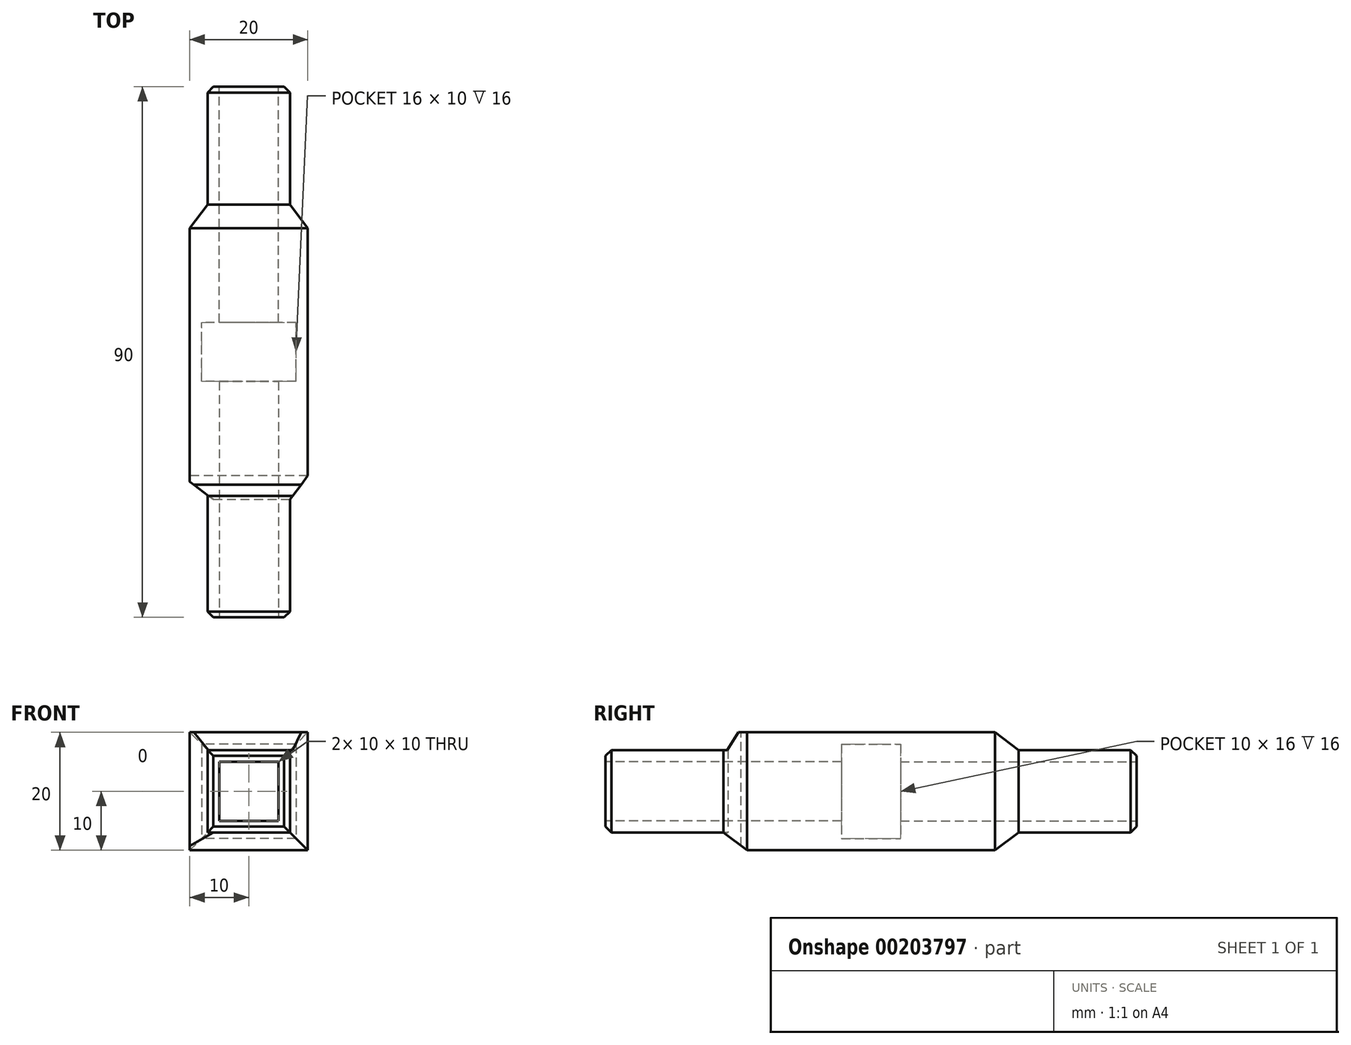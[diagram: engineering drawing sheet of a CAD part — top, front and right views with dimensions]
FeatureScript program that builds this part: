
annotation { "Feature Type Name" : "Feature", "Feature Type Description" : "" }
export const myFeature = defineFeature(function(context is Context, id is Id, definition is map)
    precondition{}
    {
        {
            var Q0;
            Q0=qCreatedBy(makeId("Front.planeOp"),FACE);
            var sketch = newSketch(context, id + "F0", { "sketchPlane" : qUnion([Q0])});
            skLineSegment(sketch, "E0.bottom", {"start": v(10, 10) * mm, "end": v(-10, 10) * mm});
            skLineSegment(sketch, "E0.top", {"start": v(10, -10) * mm, "end": v(-10, -10) * mm});
            skLineSegment(sketch, "E0.left", {"start": v(10, 10) * mm, "end": v(10, -10) * mm});
            skLineSegment(sketch, "E0.right", {"start": v(-10, 10) * mm, "end": v(-10, -10) * mm});
            skPoint(sketch, "E0.middle", {"position": v(0, 0) * mm});
            skLineSegment(sketch, "E1.0", {"start": v(-8, 8) * mm, "end": v(-8, -8) * mm});
            skLineSegment(sketch, "E1.1", {"start": v(8, 8) * mm, "end": v(-8, 8) * mm});
            skLineSegment(sketch, "E1.2", {"start": v(8, 8) * mm, "end": v(8, -8) * mm});
            skLineSegment(sketch, "E1.3", {"start": v(8, -8) * mm, "end": v(-8, -8) * mm});
            skSolve(sketch);
        }
        {
            var Q0;
            Q0=makeQuery(id+"F0.imprint","IMPRINT",FACE,{"disambiguationData":[TD([[makeQuery(id+"F0.imprint","IMPRINT",EDGE,{"derivedFrom":sQuery(id+"F0.wireOp",EDGE,"E0.bottom")}),1.0]])]});
            extrude(context, id + "F1", {"entities" : qUnion([Q0]), "depth" : 50 * mm, "symmetric" : true});
        }
        {
            var Q0;
            Q0=makeQuery(id+"F1.opExtrude","CAP_FACE",FACE,{"disambiguationData":[OSD([sQuery(id+"F0.wireOp",EDGE,"E0.bottom"),sQuery(id+"F0.wireOp",EDGE,"E0.top"),sQuery(id+"F0.wireOp",EDGE,"E0.left"),sQuery(id+"F0.wireOp",EDGE,"E0.right"),sQuery(id+"F0.wireOp",EDGE,"E1.0"),sQuery(id+"F0.wireOp",EDGE,"E1.1"),sQuery(id+"F0.wireOp",EDGE,"E1.2"),sQuery(id+"F0.wireOp",EDGE,"E1.3")])],"isStart":false});
            var sketch = newSketch(context, id + "F2", { "sketchPlane" : qUnion([Q0])});
            skLineSegment(sketch, "E2.bottom", {"start": v(-8, 8) * mm, "end": v(8, 8) * mm});
            skLineSegment(sketch, "E2.top", {"start": v(-8, -8) * mm, "end": v(8, -8) * mm});
            skLineSegment(sketch, "E2.left", {"start": v(-8, 8) * mm, "end": v(-8, -8) * mm});
            skLineSegment(sketch, "E2.right", {"start": v(8, 8) * mm, "end": v(8, -8) * mm});
            skPoint(sketch, "E2.middle", {"position": v(0, 0) * mm});
            skLineSegment(sketch, "E3.0", {"start": v(-5, 5) * mm, "end": v(5, 5) * mm});
            skLineSegment(sketch, "E3.1", {"start": v(-5, 5) * mm, "end": v(-5, -5) * mm});
            skLineSegment(sketch, "E3.2", {"start": v(-5, -5) * mm, "end": v(5, -5) * mm});
            skLineSegment(sketch, "E3.3", {"start": v(5, 5) * mm, "end": v(5, -5) * mm});
            skSolve(sketch);
        }
        {
            var Q0;
            Q0=makeQuery(id+"F2.imprint","IMPRINT",FACE,{"disambiguationData":[TD([[makeQuery(id+"F2.imprint","IMPRINT",EDGE,{"derivedFrom":sQuery(id+"F2.wireOp",EDGE,"E2.bottom")}),1.0]])]});
            extrude(context, id + "F3", {"entities" : qUnion([Q0]), "operationType" : NewBodyOperationType.ADD, "oppositeDirection" : true, "depth" : 20 * mm});
        }
        {
            var Q0;
            Q0=makeQuery(id+"F3.boolean.opBoolean","MERGE",FACE,{"derivedFrom":[makeQuery(id+"F1.opExtrude","CAP_FACE",FACE,{"disambiguationData":[OSD([sQuery(id+"F0.wireOp",EDGE,"E0.bottom"),sQuery(id+"F0.wireOp",EDGE,"E0.top"),sQuery(id+"F0.wireOp",EDGE,"E0.left"),sQuery(id+"F0.wireOp",EDGE,"E0.right"),sQuery(id+"F0.wireOp",EDGE,"E1.0"),sQuery(id+"F0.wireOp",EDGE,"E1.1"),sQuery(id+"F0.wireOp",EDGE,"E1.2"),sQuery(id+"F0.wireOp",EDGE,"E1.3")])],"isStart":false}),makeQuery(id+"F3.opExtrude","CAP_FACE",FACE,{"disambiguationData":[OSD([sQuery(id+"F2.wireOp",EDGE,"E2.bottom"),sQuery(id+"F2.wireOp",EDGE,"E2.top"),sQuery(id+"F2.wireOp",EDGE,"E2.left"),sQuery(id+"F2.wireOp",EDGE,"E2.right"),sQuery(id+"F2.wireOp",EDGE,"E3.0"),sQuery(id+"F2.wireOp",EDGE,"E3.1"),sQuery(id+"F2.wireOp",EDGE,"E3.2"),sQuery(id+"F2.wireOp",EDGE,"E3.3")])],"isStart":true})]});
            var sketch = newSketch(context, id + "F4", { "sketchPlane" : qUnion([Q0])});
            skLineSegment(sketch, "E4.bottom", {"start": v(-5, 5) * mm, "end": v(5, 5) * mm});
            skLineSegment(sketch, "E4.top", {"start": v(-5, -5) * mm, "end": v(5, -5) * mm});
            skLineSegment(sketch, "E4.left", {"start": v(-5, 5) * mm, "end": v(-5, -5) * mm});
            skLineSegment(sketch, "E4.right", {"start": v(5, 5) * mm, "end": v(5, -5) * mm});
            skPoint(sketch, "E4.middle", {"position": v(0, 0) * mm});
            skLineSegment(sketch, "E5.0", {"start": v(-7, 7) * mm, "end": v(7, 7) * mm});
            skLineSegment(sketch, "E5.1", {"start": v(-7, 7) * mm, "end": v(-7, -7) * mm});
            skLineSegment(sketch, "E5.2", {"start": v(-7, -7) * mm, "end": v(7, -7) * mm});
            skLineSegment(sketch, "E5.3", {"start": v(7, 7) * mm, "end": v(7, -7) * mm});
            skSolve(sketch);
        }
        {
            var Q0;
            Q0=makeQuery(id+"F4.imprint","IMPRINT",FACE,{"disambiguationData":[TD([[makeQuery(id+"F4.imprint","IMPRINT",EDGE,{"derivedFrom":sQuery(id+"F4.wireOp",EDGE,"E4.bottom")}),1.0]])]});
            extrude(context, id + "F5", {"entities" : qUnion([Q0]), "operationType" : NewBodyOperationType.ADD, "depth" : 20 * mm});
        }
        {
            var Q0;
            Q0=makeQuery(id+"F1.opExtrude","CAP_FACE",FACE,{"disambiguationData":[OSD([sQuery(id+"F0.wireOp",EDGE,"E0.bottom"),sQuery(id+"F0.wireOp",EDGE,"E0.top"),sQuery(id+"F0.wireOp",EDGE,"E0.left"),sQuery(id+"F0.wireOp",EDGE,"E0.right"),sQuery(id+"F0.wireOp",EDGE,"E1.0"),sQuery(id+"F0.wireOp",EDGE,"E1.1"),sQuery(id+"F0.wireOp",EDGE,"E1.2"),sQuery(id+"F0.wireOp",EDGE,"E1.3")])],"isStart":true});
            var sketch = newSketch(context, id + "F6", { "sketchPlane" : qUnion([Q0])});
            skLineSegment(sketch, "E6.bottom", {"start": v(-8, 8) * mm, "end": v(8, 8) * mm});
            skLineSegment(sketch, "E6.top", {"start": v(-8, -8) * mm, "end": v(8, -8) * mm});
            skLineSegment(sketch, "E6.left", {"start": v(-8, 8) * mm, "end": v(-8, -8) * mm});
            skLineSegment(sketch, "E6.right", {"start": v(8, 8) * mm, "end": v(8, -8) * mm});
            skPoint(sketch, "E6.middle", {"position": v(0, 0) * mm});
            skLineSegment(sketch, "E7.0", {"start": v(-5, 5) * mm, "end": v(5, 5) * mm});
            skLineSegment(sketch, "E7.1", {"start": v(-5, 5) * mm, "end": v(-5, -5) * mm});
            skLineSegment(sketch, "E7.2", {"start": v(-5, -5) * mm, "end": v(5, -5) * mm});
            skLineSegment(sketch, "E7.3", {"start": v(5, 5) * mm, "end": v(5, -5) * mm});
            skSolve(sketch);
        }
        {
            var Q0;
            Q0=makeQuery(id+"F6.imprint","IMPRINT",FACE,{"disambiguationData":[TD([[makeQuery(id+"F6.imprint","IMPRINT",EDGE,{"derivedFrom":sQuery(id+"F6.wireOp",EDGE,"E6.bottom")}),-1.0]])]});
            extrude(context, id + "F7", {"entities" : qUnion([Q0]), "operationType" : NewBodyOperationType.ADD, "oppositeDirection" : true, "depth" : 20 * mm});
        }
        {
            var Q0;
            Q0=makeQuery(id+"F7.boolean.opBoolean","MERGE",FACE,{"derivedFrom":[makeQuery(id+"F1.opExtrude","CAP_FACE",FACE,{"disambiguationData":[OSD([sQuery(id+"F0.wireOp",EDGE,"E0.bottom"),sQuery(id+"F0.wireOp",EDGE,"E0.top"),sQuery(id+"F0.wireOp",EDGE,"E0.left"),sQuery(id+"F0.wireOp",EDGE,"E0.right"),sQuery(id+"F0.wireOp",EDGE,"E1.0"),sQuery(id+"F0.wireOp",EDGE,"E1.1"),sQuery(id+"F0.wireOp",EDGE,"E1.2"),sQuery(id+"F0.wireOp",EDGE,"E1.3")])],"isStart":true}),makeQuery(id+"F7.opExtrude","CAP_FACE",FACE,{"disambiguationData":[OSD([sQuery(id+"F6.wireOp",EDGE,"E6.bottom"),sQuery(id+"F6.wireOp",EDGE,"E6.top"),sQuery(id+"F6.wireOp",EDGE,"E6.left"),sQuery(id+"F6.wireOp",EDGE,"E6.right"),sQuery(id+"F6.wireOp",EDGE,"E7.0"),sQuery(id+"F6.wireOp",EDGE,"E7.1"),sQuery(id+"F6.wireOp",EDGE,"E7.2"),sQuery(id+"F6.wireOp",EDGE,"E7.3")])],"isStart":true})]});
            var sketch = newSketch(context, id + "F8", { "sketchPlane" : qUnion([Q0])});
            skLineSegment(sketch, "E8.bottom", {"start": v(-5, 5) * mm, "end": v(5, 5) * mm});
            skLineSegment(sketch, "E8.top", {"start": v(-5, -5) * mm, "end": v(5, -5) * mm});
            skLineSegment(sketch, "E8.left", {"start": v(-5, 5) * mm, "end": v(-5, -5) * mm});
            skLineSegment(sketch, "E8.right", {"start": v(5, 5) * mm, "end": v(5, -5) * mm});
            skPoint(sketch, "E8.middle", {"position": v(0, 0) * mm});
            skLineSegment(sketch, "E9.0", {"start": v(-7, 7) * mm, "end": v(7, 7) * mm});
            skLineSegment(sketch, "E9.1", {"start": v(-7, 7) * mm, "end": v(-7, -7) * mm});
            skLineSegment(sketch, "E9.2", {"start": v(-7, -7) * mm, "end": v(7, -7) * mm});
            skLineSegment(sketch, "E9.3", {"start": v(7, 7) * mm, "end": v(7, -7) * mm});
            skSolve(sketch);
        }
        {
            var Q0;
            Q0=makeQuery(id+"F8.imprint","IMPRINT",FACE,{"disambiguationData":[TD([[makeQuery(id+"F8.imprint","IMPRINT",EDGE,{"derivedFrom":sQuery(id+"F8.wireOp",EDGE,"E8.bottom")}),1.0]])]});
            extrude(context, id + "F9", {"entities" : qUnion([Q0]), "operationType" : NewBodyOperationType.ADD, "depth" : 20 * mm});
        }
        {
            var Q0;
            Q0=makeQuery(id+"F1.opExtrude","CAP_EDGE",EDGE,{"disambiguationData":[OSD([sQuery(id+"F0.wireOp",EDGE,"E0.bottom")])],"isStart":true});
            var Q1;
            Q1=makeQuery(id+"F1.opExtrude","CAP_EDGE",EDGE,{"disambiguationData":[OSD([sQuery(id+"F0.wireOp",EDGE,"E0.left")])],"isStart":true});
            var Q2;
            Q2=makeQuery(id+"F1.opExtrude","CAP_EDGE",EDGE,{"disambiguationData":[OSD([sQuery(id+"F0.wireOp",EDGE,"E0.right")])],"isStart":true});
            var Q3;
            Q3=makeQuery(id+"F1.opExtrude","CAP_EDGE",EDGE,{"disambiguationData":[OSD([sQuery(id+"F0.wireOp",EDGE,"E0.top")])],"isStart":true});
            var Q4;
            Q4=makeQuery(id+"F1.opExtrude","CAP_EDGE",EDGE,{"disambiguationData":[OSD([sQuery(id+"F0.wireOp",EDGE,"E0.right")])],"isStart":false});
            var Q5;
            Q5=makeQuery(id+"F1.opExtrude","CAP_EDGE",EDGE,{"disambiguationData":[OSD([sQuery(id+"F0.wireOp",EDGE,"E0.left")])],"isStart":false});
            var Q6;
            Q6=makeQuery(id+"F1.opExtrude","CAP_EDGE",EDGE,{"disambiguationData":[OSD([sQuery(id+"F0.wireOp",EDGE,"E0.top")])],"isStart":false});
            chamfer(context, id + "F10", {"entities" : qUnion([Q0, Q1, Q2, Q3, Q4, Q5, Q6]), "chamferType" : ChamferType.TWO_OFFSETS, "width1" : 4 * mm, "oppositeDirection" : false, "width2" : 3 * mm, "tangentPropagation" : true});
        }
        {
            var Q0;
            Q0=makeQuery(id+"F1.opExtrude","CAP_EDGE",EDGE,{"disambiguationData":[OSD([sQuery(id+"F0.wireOp",EDGE,"E0.bottom")])],"isStart":false});
            chamfer(context, id + "F11", {"entities" : qUnion([Q0]), "chamferType" : ChamferType.TWO_OFFSETS, "width1" : 4 * mm, "oppositeDirection" : false, "width2" : 2.5 * mm, "tangentPropagation" : true});
        }
        {
            var Q0;
            Q0=makeQuery(id+"F5.opExtrude","CAP_EDGE",EDGE,{"disambiguationData":[OSD([sQuery(id+"F4.wireOp",EDGE,"E5.0")])],"isStart":false});
            var Q1;
            Q1=makeQuery(id+"F5.opExtrude","CAP_EDGE",EDGE,{"disambiguationData":[OSD([sQuery(id+"F4.wireOp",EDGE,"E5.3")])],"isStart":false});
            var Q2;
            Q2=makeQuery(id+"F5.opExtrude","CAP_EDGE",EDGE,{"disambiguationData":[OSD([sQuery(id+"F4.wireOp",EDGE,"E5.2")])],"isStart":false});
            var Q3;
            Q3=makeQuery(id+"F5.opExtrude","CAP_EDGE",EDGE,{"disambiguationData":[OSD([sQuery(id+"F4.wireOp",EDGE,"E5.1")])],"isStart":false});
            var Q4;
            Q4=makeQuery(id+"F9.opExtrude","CAP_EDGE",EDGE,{"disambiguationData":[OSD([sQuery(id+"F8.wireOp",EDGE,"E9.0")])],"isStart":false});
            var Q5;
            Q5=makeQuery(id+"F9.opExtrude","CAP_EDGE",EDGE,{"disambiguationData":[OSD([sQuery(id+"F8.wireOp",EDGE,"E9.3")])],"isStart":false});
            var Q6;
            Q6=makeQuery(id+"F9.opExtrude","CAP_EDGE",EDGE,{"disambiguationData":[OSD([sQuery(id+"F8.wireOp",EDGE,"E9.2")])],"isStart":false});
            var Q7;
            Q7=makeQuery(id+"F9.opExtrude","CAP_EDGE",EDGE,{"disambiguationData":[OSD([sQuery(id+"F8.wireOp",EDGE,"E9.1")])],"isStart":false});
            chamfer(context, id + "F12", {"entities" : qUnion([Q0, Q1, Q2, Q3, Q4, Q5, Q6, Q7]), "width" : 1 * mm, "tangentPropagation" : true});
        }
    });
